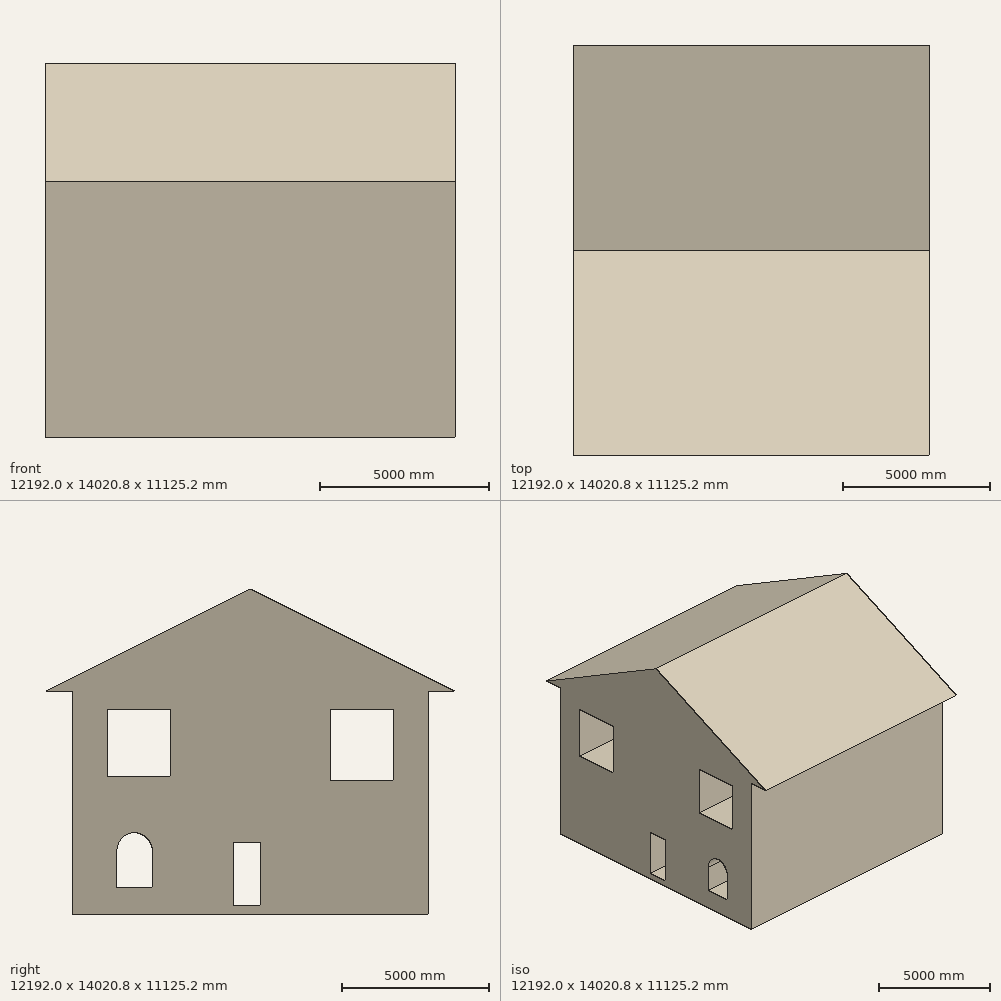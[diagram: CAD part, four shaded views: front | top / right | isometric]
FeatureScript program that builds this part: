
annotation { "Feature Type Name" : "Feature", "Feature Type Description" : "" }
export const myFeature = defineFeature(function(context is Context, id is Id, definition is map)
    precondition{}
    {
        {
            var Q0;
            Q0=qCreatedBy(makeId("Right.planeOp"),FACE);
            var sketch = newSketch(context, id + "F0", { "sketchPlane" : qUnion([Q0])});
            skLineSegment(sketch, "E0", {"start": v(0, 0) * mm, "end": v(-6096, 0) * mm});
            skLineSegment(sketch, "E1", {"start": v(0, 0) * mm, "end": v(6096, 0) * mm});
            skLineSegment(sketch, "E2", {"start": v(0, 3048) * mm, "end": v(6096, 0) * mm});
            skLineSegment(sketch, "E3", {"start": v(0, 3048) * mm, "end": v(-6096, 0) * mm});
            skLineSegment(sketch, "E4", {"start": v(-6096, 0) * mm, "end": v(-6096, -7315.2) * mm});
            skLineSegment(sketch, "E5", {"start": v(6096, 0) * mm, "end": v(6096, -7315.2) * mm});
            skLineSegment(sketch, "E6", {"start": v(-6096, -7315.2) * mm, "end": v(-6096, -7620) * mm});
            skLineSegment(sketch, "E7", {"start": v(-6096, -7620) * mm, "end": v(6096, -7620) * mm});
            skLineSegment(sketch, "E8", {"start": v(6096, -7315.2) * mm, "end": v(6096, -7620) * mm});
            skLineSegment(sketch, "E9", {"start": v(0, 3048) * mm, "end": v(0, 3505.2) * mm});
            skLineSegment(sketch, "E10", {"start": v(-6096, -7315.2) * mm, "end": v(6096, -7315.2) * mm});
            skLineSegment(sketch, "E11", {"start": v(-6096, 0) * mm, "end": v(-7010.4, 0) * mm});
            skLineSegment(sketch, "E12", {"start": v(6096, 0) * mm, "end": v(7010.4, 0) * mm});
            skLineSegment(sketch, "E13", {"start": v(-7010.4, 0) * mm, "end": v(0, 3505.2) * mm});
            skLineSegment(sketch, "E14", {"start": v(0, 3505.2) * mm, "end": v(7010.4, 0) * mm});
            skLineSegment(sketch, "E15.bottom", {"start": v(-4572, -914.4) * mm, "end": v(-3048, -914.4) * mm});
            skLineSegment(sketch, "E15.top", {"start": v(-4572, -2598.06) * mm, "end": v(-3048, -2598.06) * mm});
            skLineSegment(sketch, "E15.left", {"start": v(-4572, -914.4) * mm, "end": v(-4572, -2598.06) * mm});
            skLineSegment(sketch, "E15.right", {"start": v(-3048, -914.4) * mm, "end": v(-3048, -2598.06) * mm});
            skLineSegment(sketch, "E16.bottom", {"start": v(3048, -914.4) * mm, "end": v(4572, -914.4) * mm});
            skLineSegment(sketch, "E16.top", {"start": v(3048, -2743.2) * mm, "end": v(4572, -2743.2) * mm});
            skLineSegment(sketch, "E16.left", {"start": v(3048, -914.4) * mm, "end": v(3048, -2743.2) * mm});
            skLineSegment(sketch, "E16.right", {"start": v(4572, -914.4) * mm, "end": v(4572, -2743.2) * mm});
            skLineSegment(sketch, "E17.0", {"start": v(-4876.8, -609.6) * mm, "end": v(-2743.2, -609.6) * mm});
            skLineSegment(sketch, "E17.1", {"start": v(-4876.8, -609.6) * mm, "end": v(-4876.8, -2902.86) * mm});
            skLineSegment(sketch, "E17.2", {"start": v(-4876.8, -2902.86) * mm, "end": v(-2743.2, -2902.86) * mm});
            skLineSegment(sketch, "E17.3", {"start": v(-2743.2, -609.6) * mm, "end": v(-2743.2, -2902.86) * mm});
            skLineSegment(sketch, "E18.0", {"start": v(2743.2, -609.6) * mm, "end": v(4876.8, -609.6) * mm});
            skLineSegment(sketch, "E18.1", {"start": v(2743.2, -609.6) * mm, "end": v(2743.2, -3048) * mm});
            skLineSegment(sketch, "E18.2", {"start": v(2743.2, -3048) * mm, "end": v(4876.8, -3048) * mm});
            skLineSegment(sketch, "E18.3", {"start": v(4876.8, -609.6) * mm, "end": v(4876.8, -3048) * mm});
            skLineSegment(sketch, "E19.bottom", {"start": v(-4572, -5486.4) * mm, "end": v(-3352.8, -5486.4) * mm});
            skLineSegment(sketch, "E19.top", {"start": v(-4572, -6705.6) * mm, "end": v(-3352.8, -6705.6) * mm});
            skLineSegment(sketch, "E19.left", {"start": v(-4572, -5486.4) * mm, "end": v(-4572, -6705.6) * mm});
            skLineSegment(sketch, "E19.right", {"start": v(-3352.8, -5486.4) * mm, "end": v(-3352.8, -6705.6) * mm});
            skLineSegment(sketch, "E20.0", {"start": v(-4358.64, -5699.76) * mm, "end": v(-3566.16, -5699.76) * mm});
            skLineSegment(sketch, "E20.1", {"start": v(-4358.64, -5699.76) * mm, "end": v(-4358.64, -6492.24) * mm});
            skLineSegment(sketch, "E20.2", {"start": v(-4358.64, -6492.24) * mm, "end": v(-3566.16, -6492.24) * mm});
            skLineSegment(sketch, "E20.3", {"start": v(-3566.16, -5699.76) * mm, "end": v(-3566.16, -6492.24) * mm});
            skArc(sketch, "E21", {"start": v(-3962.4, -4826.74) * mm, "mid": v(-4396.26, -5037.3) * mm, "end": v(-4572, -5486.4) * mm});
            skPoint(sketch, "E21.startSnap0", {"position": v(-3962.4, -5486.4) * mm});
            skArc(sketch, "E22", {"start": v(-3352.8, -5486.4) * mm, "mid": v(-3528.54, -5037.3) * mm, "end": v(-3962.4, -4826.74) * mm});
            skLineSegment(sketch, "E23", {"start": v(-570.9, -5181.55) * mm, "end": v(-570.9, -7315.15) * mm});
            skLineSegment(sketch, "E24", {"start": v(-570.9, -5181.55) * mm, "end": v(343.5, -5181.55) * mm});
            skLineSegment(sketch, "E25", {"start": v(343.5, -5181.55) * mm, "end": v(343.5, -7315.15) * mm});
            skLineSegment(sketch, "E26", {"start": v(-570.9, -7315.15) * mm, "end": v(343.5, -7315.15) * mm});
            skSolve(sketch);
        }
        {
            var Q0;
            Q0=makeQuery(id+"F0.imprint","IMPRINT",FACE,{"disambiguationData":[TD([[makeQuery(id+"F0.imprint","IMPRINT",EDGE,{"derivedFrom":sQuery(id+"F0.wireOp",EDGE,"E19.bottom")}),-1.0]])]});
            var Q1;
            Q1=makeQuery(id+"F0.imprint","IMPRINT",FACE,{"disambiguationData":[TD([[makeQuery(id+"F0.imprint","IMPRINT",EDGE,{"derivedFrom":sQuery(id+"F0.wireOp",EDGE,"E0")}),-1.0]])]});
            var Q2;
            Q2=makeQuery(id+"F0.imprint","IMPRINT",FACE,{"disambiguationData":[TD([[makeQuery(id+"F0.imprint","IMPRINT",EDGE,{"derivedFrom":sQuery(id+"F0.wireOp",EDGE,"E19.bottom")}),1.0]])]});
            var Q3;
            Q3=makeQuery(id+"F0.imprint","IMPRINT",FACE,{"disambiguationData":[TD([[makeQuery(id+"F0.imprint","IMPRINT",EDGE,{"derivedFrom":sQuery(id+"F0.wireOp",EDGE,"E16.bottom")}),1.0]])]});
            var Q4;
            Q4=makeQuery(id+"F0.imprint","IMPRINT",FACE,{"disambiguationData":[TD([[makeQuery(id+"F0.imprint","IMPRINT",EDGE,{"derivedFrom":sQuery(id+"F0.wireOp",EDGE,"E0")}),1.0]])]});
            var Q5;
            Q5=makeQuery(id+"F0.imprint","IMPRINT",FACE,{"disambiguationData":[TD([[makeQuery(id+"F0.imprint","IMPRINT",EDGE,{"derivedFrom":sQuery(id+"F0.wireOp",EDGE,"E15.bottom")}),1.0]])]});
            var Q6;
            Q6=makeQuery(id+"F0.imprint","IMPRINT",FACE,{"disambiguationData":[TD([[makeQuery(id+"F0.imprint","IMPRINT",EDGE,{"derivedFrom":sQuery(id+"F0.wireOp",EDGE,"E3")}),-1.0]])]});
            var Q7;
            Q7=makeQuery(id+"F0.imprint","IMPRINT",FACE,{"disambiguationData":[TD([[makeQuery(id+"F0.imprint","IMPRINT",EDGE,{"derivedFrom":sQuery(id+"F0.wireOp",EDGE,"E2")}),1.0]])]});
            var Q8;
            Q8=makeQuery(id+"F0.imprint","IMPRINT",FACE,{"disambiguationData":[TD([[makeQuery(id+"F0.imprint","IMPRINT",EDGE,{"derivedFrom":sQuery(id+"F0.wireOp",EDGE,"E20.0")}),-1.0]])]});
            var Q9;
            Q9=makeQuery(id+"F0.imprint","IMPRINT",FACE,{"disambiguationData":[TD([[makeQuery(id+"F0.imprint","IMPRINT",EDGE,{"derivedFrom":sQuery(id+"F0.wireOp",EDGE,"E16.bottom")}),-1.0]])]});
            var Q10;
            Q10=makeQuery(id+"F0.imprint","IMPRINT",FACE,{"disambiguationData":[TD([[makeQuery(id+"F0.imprint","IMPRINT",EDGE,{"derivedFrom":sQuery(id+"F0.wireOp",EDGE,"E15.bottom")}),-1.0]])]});
            var Q11;
            Q11=makeQuery(id+"F0.imprint","IMPRINT",FACE,{"disambiguationData":[TD([[makeQuery(id+"F0.imprint","IMPRINT",EDGE,{"derivedFrom":sQuery(id+"F0.wireOp",EDGE,"E6")}),1.0]])]});
            extrude(context, id + "F1", {"entities" : qUnion([Q0, Q1, Q2, Q3, Q4, Q5, Q6, Q7, Q8, Q9, Q10, Q11]), "depth" : 12192 * mm, "offsetDistance" : 30.48 * mm});
        }
        {
            var Q0;
            Q0 = qSketchRegion(id + "F0", true);
            extrude(context, id + "F2", {"entities" : qUnion([Q0]), "operationType" : NewBodyOperationType.INTERSECT, "depth" : 12222.48 * mm, "offsetDistance" : 30.48 * mm});
        }
    });
